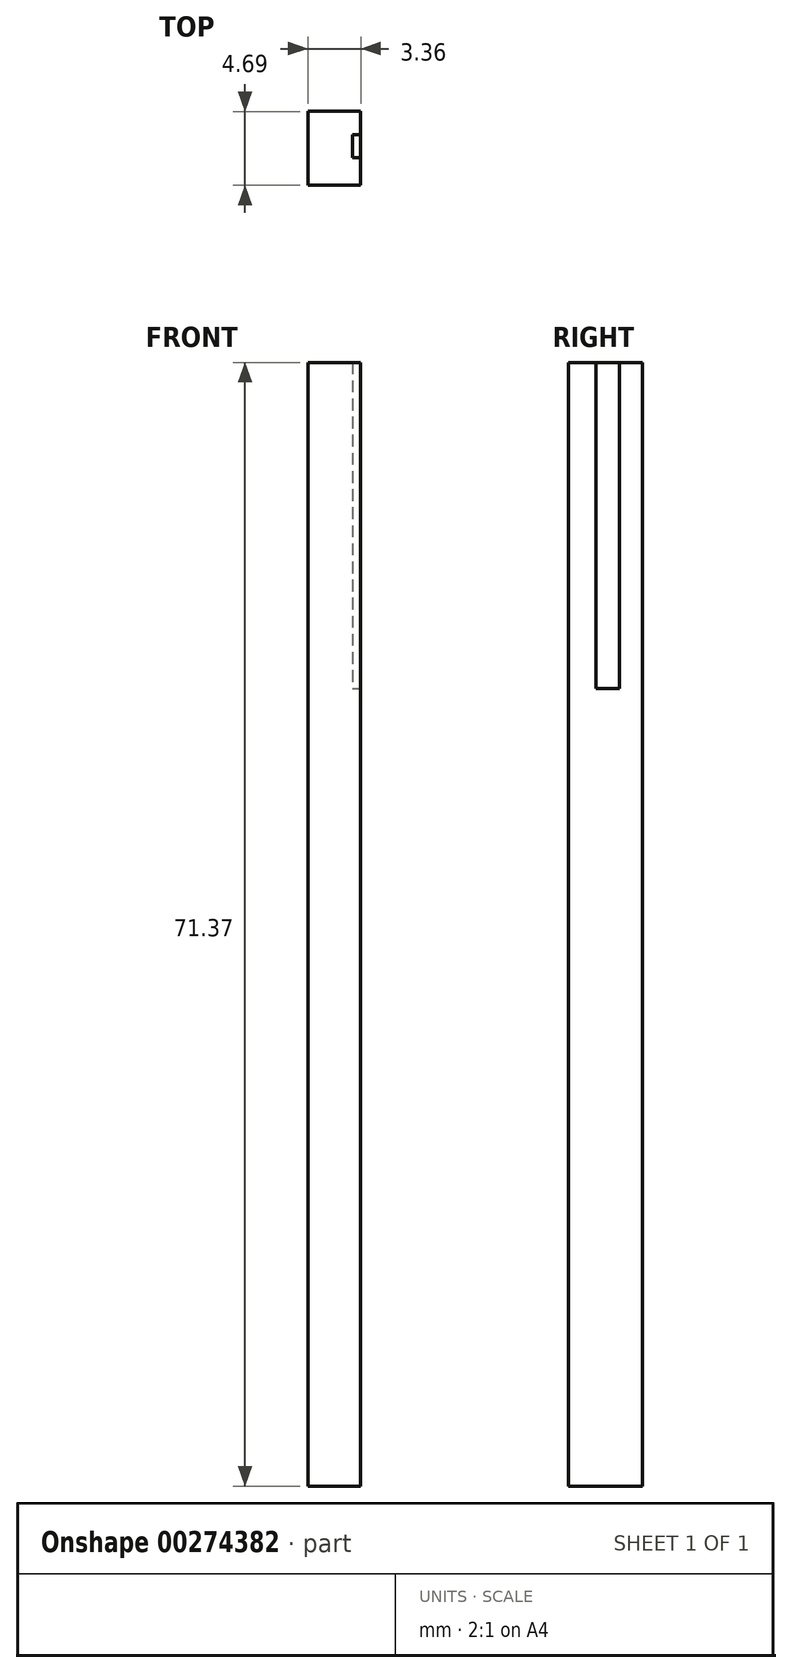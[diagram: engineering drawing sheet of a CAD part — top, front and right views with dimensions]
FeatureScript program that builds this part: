
annotation { "Feature Type Name" : "Feature", "Feature Type Description" : "" }
export const myFeature = defineFeature(function(context is Context, id is Id, definition is map)
    precondition{}
    {
        {
            var Q0;
            Q0=qCreatedBy(makeId("Top.planeOp"),FACE);
            var sketch = newSketch(context, id + "F0", { "sketchPlane" : qUnion([Q0])});
            skLineSegment(sketch, "E0.bottom", {"start": v(-45.35, 35.15) * mm, "end": v(-42, 35.15) * mm});
            skLineSegment(sketch, "E0.top", {"start": v(-45.35, 39.84) * mm, "end": v(-42, 39.84) * mm});
            skLineSegment(sketch, "E0.left", {"start": v(-45.35, 39.84) * mm, "end": v(-45.35, 35.15) * mm});
            skLineSegment(sketch, "E0.right", {"start": v(-42, 39.84) * mm, "end": v(-42, 35.15) * mm});
            skSolve(sketch);
        }
        {
            var Q0;
            Q0 = qSketchRegion(id + "F0", true);
            extrude(context, id + "F1", {"entities" : qUnion([Q0]), "depth" : 71.37 * mm});
        }
        {
            var Q0;
            Q0=makeQuery(id+"F1.opExtrude","SWEPT_FACE",FACE,{"disambiguationData":[OSD([sQuery(id+"F0.wireOp",EDGE,"E0.right")])]});
            var sketch = newSketch(context, id + "F2", { "sketchPlane" : qUnion([Q0])});
            skPoint(sketch, "E1.endSnap0", {"position": v(37.5, 71.37) * mm});
            skLineSegment(sketch, "E2", {"start": v(36.9, 71.37) * mm, "end": v(36.9, 50.67) * mm});
            skLineSegment(sketch, "E3", {"start": v(36.9, 50.67) * mm, "end": v(38.38, 50.67) * mm});
            skLineSegment(sketch, "E4", {"start": v(38.38, 50.67) * mm, "end": v(38.38, 71.37) * mm});
            skLineSegment(sketch, "E5", {"start": v(38.38, 71.37) * mm, "end": v(36.9, 71.37) * mm});
            skSolve(sketch);
        }
        {
            var Q0;
            Q0 = qSketchRegion(id + "F2", true);
            extrude(context, id + "F3", {"entities" : qUnion([Q0]), "operationType" : NewBodyOperationType.REMOVE, "oppositeDirection" : true, "depth" : 0.5 * mm});
        }
    });
